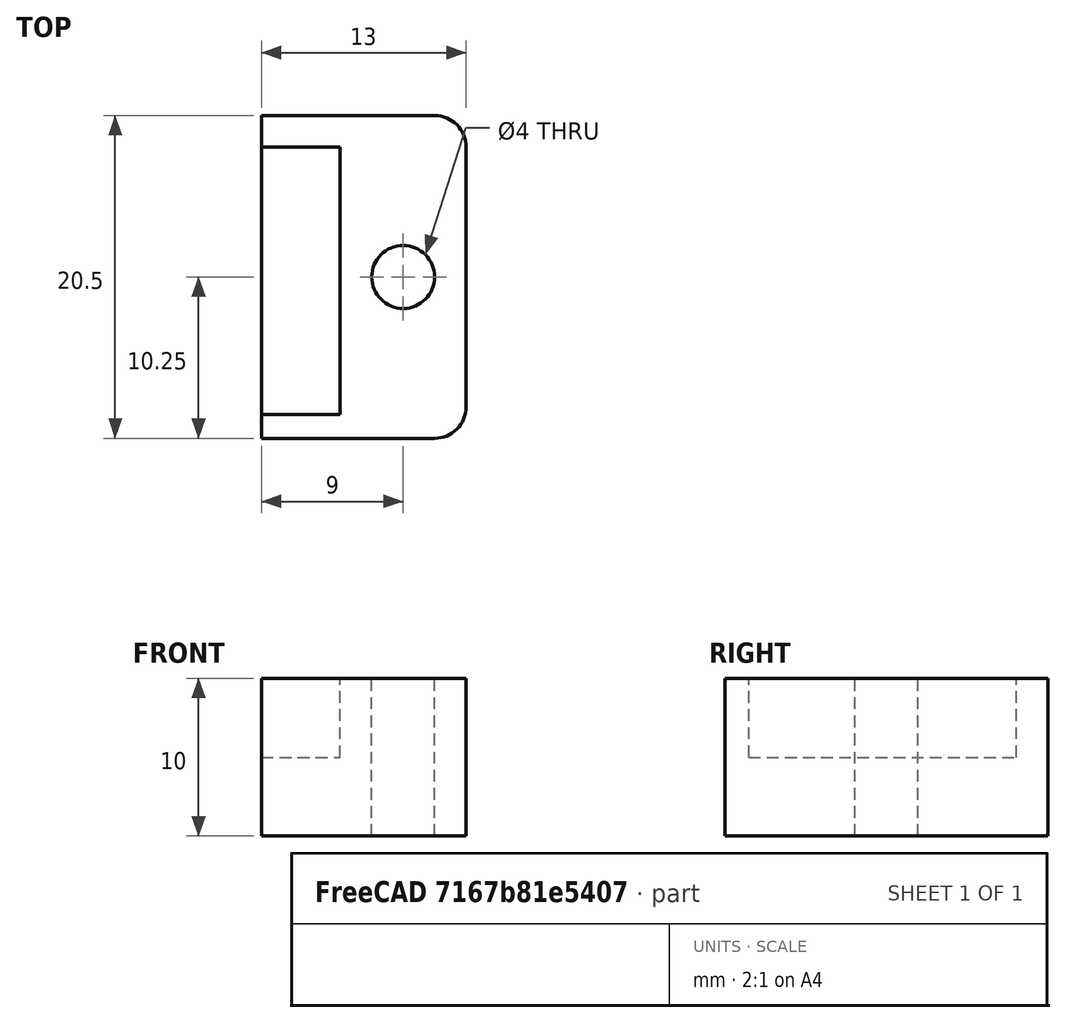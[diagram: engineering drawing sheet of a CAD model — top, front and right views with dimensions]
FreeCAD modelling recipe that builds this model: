
FCSTD DOCUMENT  (FreeCAD 0.19R)
Label: Caliper300mmEndCap
License: All rights reserved
LicenseURL: http://en.wikipedia.org/wiki/All_rights_reserved
objects: Part::Box×2, Part::Cut×2, Part::Cylinder×1, Part::Fillet×1
note: 6 computed .brp shape members not serialized (recipe doc carries the construction recipe); baked Part::Feature solids carry a one-line shape summary decoded from their .brp

FEATURE [Part::Box] Box  label="Cube"
  AttacherType = Attacher::AttachEngine3D
  Height = 5
  Length = 5
  Placement = pos=(0,1.5,5) rot=(0,0,1;0rad)
  Width = 17
FEATURE [Part::Box] Box001  label="Cube001"
  AttacherType = Attacher::AttachEngine3D
  Height = 10
  Length = 13
  Width = 20.5
FEATURE [Part::Cylinder] Cylinder
  Angle = 360
  AttacherType = Attacher::AttachEngine3D
  Height = 10
  Placement = pos=(9,10.25,0) rot=(0,0,1;0rad)
  Radius = 2
FEATURE [Part::Cut] Cut
  Base = -> Box001
  Tool = -> Box
FEATURE [Part::Cut] Cut001
  Base = -> Cut
  Tool = -> Cylinder
FEATURE [Part::Fillet] Fillet
  Base = -> Cut001
  Edges = 2 edges r=2: [Edge22,Edge26]
